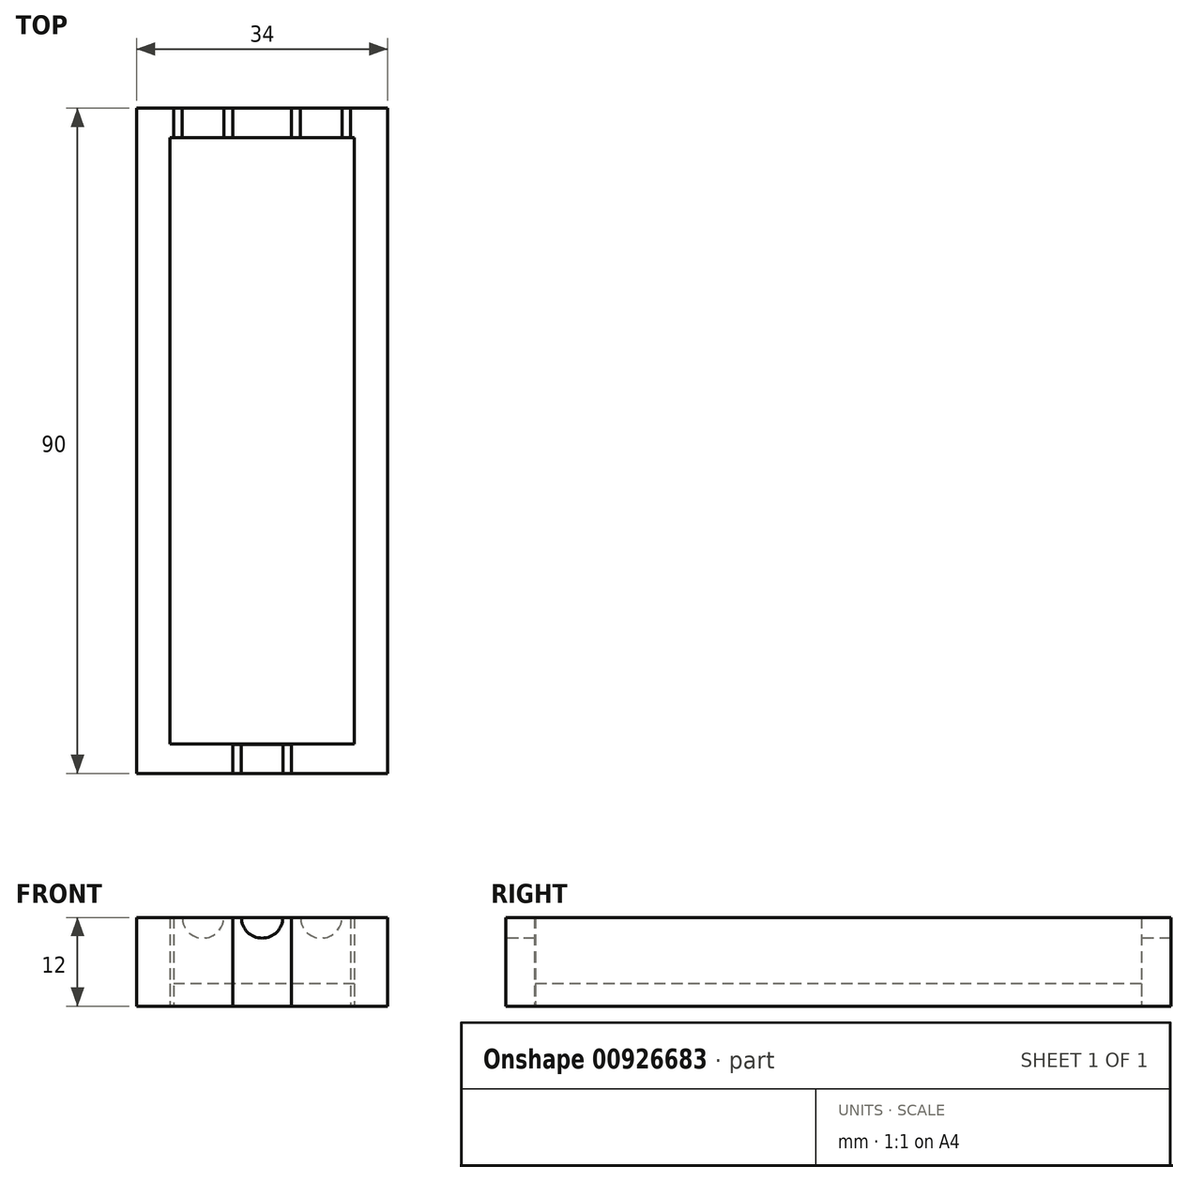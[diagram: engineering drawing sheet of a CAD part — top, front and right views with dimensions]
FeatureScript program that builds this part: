
annotation { "Feature Type Name" : "Feature", "Feature Type Description" : "" }
export const myFeature = defineFeature(function(context is Context, id is Id, definition is map)
    precondition{}
    {
        {
            var Q0;
            Q0=qCreatedBy(makeId("Top.planeOp"),FACE);
            var sketch = newSketch(context, id + "F0", { "sketchPlane" : qUnion([Q0])});
            skLineSegment(sketch, "E0.bottom", {"start": v(17, -45) * mm, "end": v(-17, -45) * mm});
            skLineSegment(sketch, "E0.top", {"start": v(17, 45) * mm, "end": v(-17, 45) * mm});
            skLineSegment(sketch, "E0.left", {"start": v(17, -45) * mm, "end": v(17, 45) * mm});
            skLineSegment(sketch, "E0.right", {"start": v(-17, -45) * mm, "end": v(-17, 45) * mm});
            skPoint(sketch, "E0.middle", {"position": v(0, 0) * mm});
            skLineSegment(sketch, "E1.bottom", {"start": v(12.5, 41) * mm, "end": v(-12.5, 41) * mm});
            skLineSegment(sketch, "E1.top", {"start": v(12.5, -41) * mm, "end": v(-12.5, -41) * mm});
            skLineSegment(sketch, "E1.left", {"start": v(12.5, 41) * mm, "end": v(12.5, -41) * mm});
            skLineSegment(sketch, "E1.right", {"start": v(-12.5, 41) * mm, "end": v(-12.5, -41) * mm});
            skLineSegment(sketch, "E2.bottom", {"start": v(4, -45) * mm, "end": v(-4, -45) * mm});
            skLineSegment(sketch, "E2.top", {"start": v(4, -41.12) * mm, "end": v(-4, -41.12) * mm});
            skLineSegment(sketch, "E2.left", {"start": v(4, -45) * mm, "end": v(4, -41.12) * mm});
            skLineSegment(sketch, "E2.right", {"start": v(-4, -45) * mm, "end": v(-4, -41.12) * mm});
            skPoint(sketch, "E2.middle", {"position": v(0, -43.06) * mm});
            skPoint(sketch, "E2.middle.positionSnap0", {"position": v(0, -41) * mm});
            skPoint(sketch, "E2.centerSnap0", {"position": v(0, -41) * mm});
            skLineSegment(sketch, "E3.bottom", {"start": v(4, 41) * mm, "end": v(-4, 41) * mm});
            skLineSegment(sketch, "E3.top", {"start": v(4, 45) * mm, "end": v(-4, 45) * mm});
            skLineSegment(sketch, "E3.left", {"start": v(4, 41) * mm, "end": v(4, 45) * mm});
            skLineSegment(sketch, "E3.right", {"start": v(-4, 41) * mm, "end": v(-4, 45) * mm});
            skPoint(sketch, "E3.middle", {"position": v(0, 43) * mm});
            skLineSegment(sketch, "E4.bottom", {"start": v(-4, 45) * mm, "end": v(-12, 45) * mm});
            skLineSegment(sketch, "E4.top", {"start": v(-4, 41) * mm, "end": v(-12, 41) * mm});
            skLineSegment(sketch, "E4.left", {"start": v(-4, 45) * mm, "end": v(-4, 41) * mm});
            skLineSegment(sketch, "E4.right", {"start": v(-12, 45) * mm, "end": v(-12, 41) * mm});
            skLineSegment(sketch, "E5.bottom", {"start": v(4, 45) * mm, "end": v(12, 45) * mm});
            skLineSegment(sketch, "E5.top", {"start": v(4, 41) * mm, "end": v(12, 41) * mm});
            skLineSegment(sketch, "E5.left", {"start": v(4, 45) * mm, "end": v(4, 41) * mm});
            skLineSegment(sketch, "E5.right", {"start": v(12, 45) * mm, "end": v(12, 41) * mm});
            skLineSegment(sketch, "E6.bottom", {"start": v(-12.5, -41) * mm, "end": v(12.5, -41) * mm});
            skLineSegment(sketch, "E6.top", {"start": v(-12.5, 41) * mm, "end": v(12.5, 41) * mm});
            skLineSegment(sketch, "E6.left", {"start": v(-12.5, -41) * mm, "end": v(-12.5, 41) * mm});
            skLineSegment(sketch, "E6.right", {"start": v(12.5, -41) * mm, "end": v(12.5, 41) * mm});
            skLineSegment(sketch, "E7.bottom", {"start": v(12.5, 41) * mm, "end": v(4, 41) * mm});
            skLineSegment(sketch, "E7.top", {"start": v(12.5, 45) * mm, "end": v(4, 45) * mm});
            skLineSegment(sketch, "E7.left", {"start": v(12.5, 41) * mm, "end": v(12.5, 45) * mm});
            skLineSegment(sketch, "E8.right", {"start": v(-12, 41) * mm, "end": v(-12, 45) * mm});
            skSolve(sketch);
        }
        {
            var Q0;
            Q0=makeQuery(id+"F0.imprint","IMPRINT",FACE,{"disambiguationData":[TD([[makeQuery(id+"F0.imprint","IMPRINT",EDGE,{"derivedFrom":sQuery(id+"F0.wireOp",EDGE,"E2.top")}),1.0]])]});
            var Q1;
            {var subQ0=sQuery(id+"F0.wireOp",EDGE,"E3.right");Q1=makeQuery(id+"F0.imprint","IMPRINT",FACE,{"disambiguationData":[TD([[makeQuery(id+"F0.imprint","IMPRINT",EDGE,{"derivedFrom":subQ0}),1.0]])]});}
            var Q2;
            {var subQ2=sQuery(id+"F0.wireOp",EDGE,"E3.left");Q2=makeQuery(id+"F0.imprint","IMPRINT",FACE,{"disambiguationData":[TD([[makeQuery(id+"F0.imprint","IMPRINT",EDGE,{"derivedFrom":subQ2}),-1.0]])]});}
            extrude(context, id + "F1", {"entities" : qUnion([Q0, Q1, Q2]), "depth" : 12 * mm, "offsetDistance" : 25 * mm});
        }
        {
            var Q0;
            Q0=makeQuery(id+"F1.opExtrude","SWEPT_FACE",FACE,{"disambiguationData":[OSD([sQuery(id+"F0.wireOp",EDGE,"E0.bottom")])]});
            var sketch = newSketch(context, id + "F2", { "sketchPlane" : qUnion([Q0])});
            skArc(sketch, "E9", {"start": v(-4, 12) * mm, "mid": v(0, 8) * mm, "end": v(4, 12) * mm});
            skSolve(sketch);
        }
        {
            var Q0;
            {var subQ10=makeQuery(id+"F0.imprint","IMPRINT",EDGE,{"derivedFrom":sQuery(id+"F0.wireOp",EDGE,"E2.top")});Q0=qUnion([makeQuery(id+"F0.imprint","IMPRINT",FACE,{"disambiguationData":[TD([[subQ10,1.0]])]}),makeQuery(id+"F0.imprint","IMPRINT",FACE,{"disambiguationData":[TD([[makeQuery(id+"F0.imprint","IMPRINT",EDGE,{"derivedFrom":sQuery(id+"F0.wireOp",EDGE,"E0.top")}),1.0]])]})]);}
            var Q1;
            {var subQ0=sQuery(id+"F0.wireOp",EDGE,"E5.right");Q1=makeQuery(id+"F0.imprint","IMPRINT",FACE,{"disambiguationData":[TD([[makeQuery(id+"F0.imprint","IMPRINT",EDGE,{"derivedFrom":subQ0}),1.0]])]});}
            var Q2;
            Q2=makeQuery(id+"F0.imprint","IMPRINT",FACE,{"disambiguationData":[TD([[makeQuery(id+"F0.imprint","IMPRINT",EDGE,{"derivedFrom":sQuery(id+"F0.wireOp",EDGE,"E3.top")}),1.0]])]});
            extrude(context, id + "F3", {"entities" : qUnion([Q0, Q1, Q2]), "depth" : 12 * mm, "offsetDistance" : 25 * mm});
        }
        {
            var Q0;
            Q0=sQuery(id+"F2.wireOp",VERTEX,"E9.center");
            var Q1;
            Q1=makeQuery(id+"F1.opExtrude","SWEPT_BODY",BODY,{"disambiguationData":[OSD([sQuery(id+"F0.wireOp",EDGE,"E0.bottom"),sQuery(id+"F0.wireOp",EDGE,"E2.top"),sQuery(id+"F0.wireOp",EDGE,"E2.left"),sQuery(id+"F0.wireOp",EDGE,"E2.right")])]});
            var Q2;
            Q2=makeQuery(id+"F3.opExtrude","SWEPT_BODY",BODY,{"disambiguationData":[OSD([sQuery(id+"F0.wireOp",EDGE,"E0.bottom"),sQuery(id+"F0.wireOp",EDGE,"E0.top"),sQuery(id+"F0.wireOp",EDGE,"E0.left"),sQuery(id+"F0.wireOp",EDGE,"E0.right"),sQuery(id+"F0.wireOp",EDGE,"E1.bottom"),sQuery(id+"F0.wireOp",EDGE,"E1.top"),sQuery(id+"F0.wireOp",EDGE,"E1.left"),sQuery(id+"F0.wireOp",EDGE,"E1.right"),sQuery(id+"F0.wireOp",EDGE,"E3.left"),sQuery(id+"F0.wireOp",EDGE,"E3.right"),sQuery(id+"F0.wireOp",EDGE,"E4.bottom"),sQuery(id+"F0.wireOp",EDGE,"E4.right"),sQuery(id+"F0.wireOp",EDGE,"E5.bottom"),sQuery(id+"F0.wireOp",EDGE,"E5.right")])]});
            hole(context, id + "F4", {"style" : HoleStyle.SIMPLE, "endStyle" : HoleEndStyle.BLIND, "holeDiameter" : 5.6 * mm, "majorDiameter" : 5 * mm, "holeDepth" : 20 * mm, "isTappedThrough" : true, "tappedDepth" : 12 * mm, "tapClearance" : 3, "locations" : qUnion([Q0]), "scope" : qUnion([Q1, Q2])});
        }
        {
            var Q0;
            {var subQ0=sQuery(id+"F0.wireOp",EDGE,"E1.bottom");Q0=makeQuery(id+"F1.opExtrude","SWEPT_FACE",FACE,{"disambiguationData":[OSD([subQ0]),TDD([makeQuery(id+"F0.imprint","IMPRINT",EDGE,{"disambiguationData":[TD([[makeQuery(id+"F0.imprint","INTERSECT",VERTEX,{"derivedFrom":[subQ0,sQuery(id+"F0.wireOp",EDGE,"E5.right")]}),-1.0]])],"derivedFrom":subQ0})])]});}
            var sketch = newSketch(context, id + "F5", { "sketchPlane" : qUnion([Q0])});
            skArc(sketch, "E10", {"start": v(4, 12) * mm, "mid": v(8, 8) * mm, "end": v(12, 12) * mm});
            skSolve(sketch);
        }
        {
            var Q0;
            {var subQ0=sQuery(id+"F0.wireOp",EDGE,"E1.bottom");Q0=makeQuery(id+"F1.opExtrude","SWEPT_FACE",FACE,{"disambiguationData":[OSD([subQ0]),TDD([makeQuery(id+"F0.imprint","IMPRINT",EDGE,{"disambiguationData":[TD([[makeQuery(id+"F0.imprint","INTERSECT",VERTEX,{"derivedFrom":[subQ0,sQuery(id+"F0.wireOp",EDGE,"E3.right")]}),-1.0]])],"derivedFrom":subQ0})])]});}
            var sketch = newSketch(context, id + "F6", { "sketchPlane" : qUnion([Q0])});
            skArc(sketch, "E11", {"start": v(-12, 12) * mm, "mid": v(-8, 8) * mm, "end": v(-4, 12) * mm});
            skSolve(sketch);
        }
        {
            var Q0;
            Q0=sQuery(id+"F5.wireOp",VERTEX,"E10.center");
            var Q1;
            Q1=makeQuery(id+"F3.opExtrude","SWEPT_BODY",BODY,{"disambiguationData":[OSD([sQuery(id+"F0.wireOp",EDGE,"E0.bottom"),sQuery(id+"F0.wireOp",EDGE,"E0.top"),sQuery(id+"F0.wireOp",EDGE,"E0.left"),sQuery(id+"F0.wireOp",EDGE,"E0.right"),sQuery(id+"F0.wireOp",EDGE,"E1.bottom"),sQuery(id+"F0.wireOp",EDGE,"E1.top"),sQuery(id+"F0.wireOp",EDGE,"E1.left"),sQuery(id+"F0.wireOp",EDGE,"E1.right"),sQuery(id+"F0.wireOp",EDGE,"E3.left"),sQuery(id+"F0.wireOp",EDGE,"E3.right"),sQuery(id+"F0.wireOp",EDGE,"E4.bottom"),sQuery(id+"F0.wireOp",EDGE,"E4.right"),sQuery(id+"F0.wireOp",EDGE,"E5.bottom"),sQuery(id+"F0.wireOp",EDGE,"E5.right")])]});
            var Q2;
            Q2=makeQuery(id+"F1.opExtrude","SWEPT_BODY",BODY,{"disambiguationData":[OSD([sQuery(id+"F0.wireOp",EDGE,"E1.bottom"),sQuery(id+"F0.wireOp",EDGE,"E3.left"),sQuery(id+"F0.wireOp",EDGE,"E5.bottom"),sQuery(id+"F0.wireOp",EDGE,"E5.right")])]});
            hole(context, id + "F7", {"style" : HoleStyle.SIMPLE, "endStyle" : HoleEndStyle.BLIND, "holeDiameter" : 5.6 * mm, "majorDiameter" : 5 * mm, "holeDepth" : 20 * mm, "isTappedThrough" : true, "tappedDepth" : 12 * mm, "tapClearance" : 3, "startFromSketch" : true, "locations" : qUnion([Q0]), "scope" : qUnion([Q1, Q2])});
        }
        {
            var Q0;
            Q0=sQuery(id+"F6.wireOp",VERTEX,"E11.center");
            var Q1;
            Q1=makeQuery(id+"F3.opExtrude","SWEPT_BODY",BODY,{"disambiguationData":[OSD([sQuery(id+"F0.wireOp",EDGE,"E0.bottom"),sQuery(id+"F0.wireOp",EDGE,"E0.top"),sQuery(id+"F0.wireOp",EDGE,"E0.left"),sQuery(id+"F0.wireOp",EDGE,"E0.right"),sQuery(id+"F0.wireOp",EDGE,"E1.bottom"),sQuery(id+"F0.wireOp",EDGE,"E1.top"),sQuery(id+"F0.wireOp",EDGE,"E1.left"),sQuery(id+"F0.wireOp",EDGE,"E1.right"),sQuery(id+"F0.wireOp",EDGE,"E3.left"),sQuery(id+"F0.wireOp",EDGE,"E3.right"),sQuery(id+"F0.wireOp",EDGE,"E4.bottom"),sQuery(id+"F0.wireOp",EDGE,"E4.right"),sQuery(id+"F0.wireOp",EDGE,"E5.bottom"),sQuery(id+"F0.wireOp",EDGE,"E5.right")])]});
            var Q2;
            Q2=makeQuery(id+"F1.opExtrude","SWEPT_BODY",BODY,{"disambiguationData":[OSD([sQuery(id+"F0.wireOp",EDGE,"E1.bottom"),sQuery(id+"F0.wireOp",EDGE,"E3.right"),sQuery(id+"F0.wireOp",EDGE,"E4.bottom"),sQuery(id+"F0.wireOp",EDGE,"E4.right")])]});
            hole(context, id + "F8", {"style" : HoleStyle.SIMPLE, "endStyle" : HoleEndStyle.BLIND, "holeDiameter" : 5.6 * mm, "majorDiameter" : 5 * mm, "holeDepth" : 20 * mm, "isTappedThrough" : true, "tappedDepth" : 12 * mm, "tapClearance" : 3, "startFromSketch" : true, "locations" : qUnion([Q0]), "scope" : qUnion([Q1, Q2])});
        }
        {
            var Q0;
            Q0=makeQuery(id+"F0.imprint","IMPRINT",FACE,{"disambiguationData":[TD([[makeQuery(id+"F0.imprint","IMPRINT",EDGE,{"derivedFrom":sQuery(id+"F0.wireOp",EDGE,"E1.top")}),-1.0]])]});
            extrude(context, id + "F9", {"entities" : qUnion([Q0]), "depth" : 3 * mm, "offsetDistance" : 25 * mm});
        }
    });
